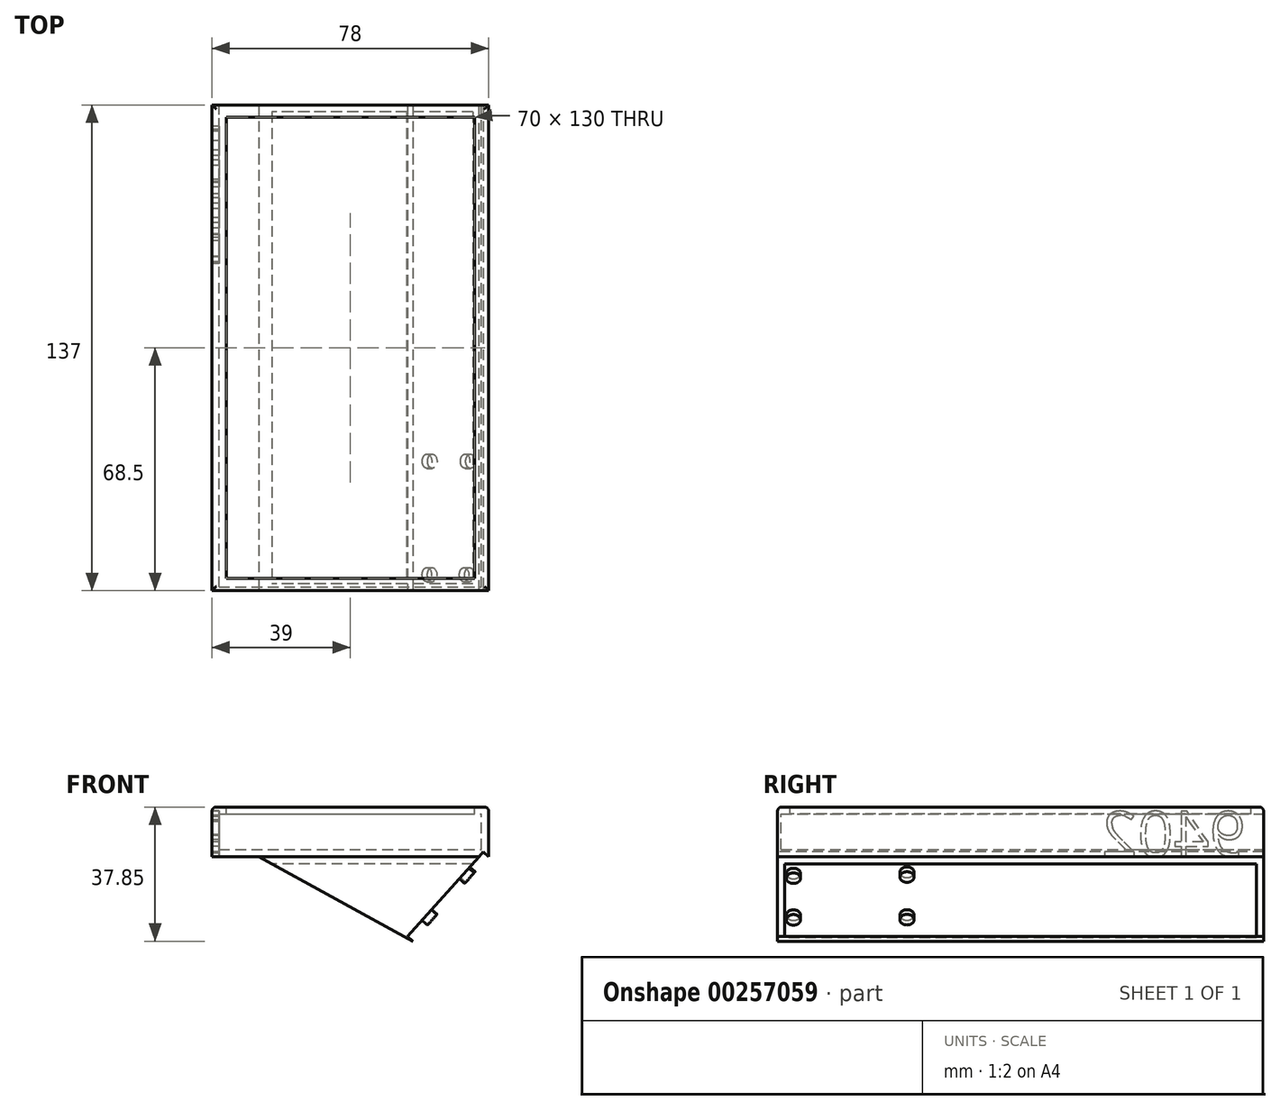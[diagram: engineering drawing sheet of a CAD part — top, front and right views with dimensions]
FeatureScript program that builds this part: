
annotation { "Feature Type Name" : "Feature", "Feature Type Description" : "" }
export const myFeature = defineFeature(function(context is Context, id is Id, definition is map)
    precondition{}
    {
        {
            var Q0;
            Q0=qCreatedBy(makeId("Top.planeOp"),FACE);
            var sketch = newSketch(context, id + "F0", { "sketchPlane" : qUnion([Q0])});
            skLineSegment(sketch, "E0.bottom", {"start": v(39, 68.5) * mm, "end": v(-39, 68.5) * mm});
            skLineSegment(sketch, "E0.top", {"start": v(39, -68.5) * mm, "end": v(-39, -68.5) * mm});
            skLineSegment(sketch, "E0.left", {"start": v(39, 68.5) * mm, "end": v(39, -68.5) * mm});
            skLineSegment(sketch, "E0.right", {"start": v(-39, 68.5) * mm, "end": v(-39, -68.5) * mm});
            skPoint(sketch, "E0.middle", {"position": v(0, 0) * mm});
            skSolve(sketch);
        }
        {
            var Q0;
            Q0 = qSketchRegion(id + "F0", true);
            extrude(context, id + "F1", {"entities" : qUnion([Q0]), "endBound" : BoundingType.SYMMETRIC, "depth" : 14 * mm});
        }
        {
            var Q0;
            Q0=makeQuery(id+"F1.opExtrude","SWEPT_FACE",FACE,{"disambiguationData":[OSD([sQuery(id+"F0.wireOp",EDGE,"E0.top")])]});
            var sketch = newSketch(context, id + "F2", { "sketchPlane" : qUnion([Q0])});
            skLineSegment(sketch, "E1", {"start": v(39, -7) * mm, "end": v(17.67, -30.85) * mm});
            skLineSegment(sketch, "E2", {"start": v(17.67, -30.85) * mm, "end": v(-25.8, -7) * mm});
            skSolve(sketch);
        }
        {
            var Q0;
            Q0 = qSketchRegion(id + "F2", true);
            var Q1;
            {var subQ0=sQuery(id+"F2.wireOp",EDGE,"E1");Q1=makeQuery(id+"F2.imprint","IMPRINT",FACE,{"disambiguationData":[TD([[makeQuery(id+"F2.imprint","IMPRINT",EDGE,{"derivedFrom":subQ0}),-1.0]])]});}
            extrude(context, id + "F3", {"entities" : qUnion([Q0, Q1]), "oppositeDirection" : true, "depth" : 137 * mm});
        }
        {
            var Q0;
            Q0=makeQuery(id+"F1.opExtrude","CAP_FACE",FACE,{"disambiguationData":[OSD([sQuery(id+"F0.wireOp",EDGE,"E0.bottom"),sQuery(id+"F0.wireOp",EDGE,"E0.top"),sQuery(id+"F0.wireOp",EDGE,"E0.left"),sQuery(id+"F0.wireOp",EDGE,"E0.right")])],"isStart":false});
            var sketch = newSketch(context, id + "F4", { "sketchPlane" : qUnion([Q0])});
            skLineSegment(sketch, "E3.bottom", {"start": v(35, -65) * mm, "end": v(-35, -65) * mm});
            skLineSegment(sketch, "E3.top", {"start": v(35, 65) * mm, "end": v(-35, 65) * mm});
            skLineSegment(sketch, "E3.left", {"start": v(35, -65) * mm, "end": v(35, 65) * mm});
            skLineSegment(sketch, "E3.right", {"start": v(-35, -65) * mm, "end": v(-35, 65) * mm});
            skPoint(sketch, "E3.middle", {"position": v(0, 0) * mm});
            skSolve(sketch);
        }
        {
            var Q0;
            Q0 = qSketchRegion(id + "F4", true);
            extrude(context, id + "F5", {"entities" : qUnion([Q0]), "operationType" : NewBodyOperationType.REMOVE, "oppositeDirection" : true, "depth" : 12 * mm});
        }
        {
            var Q0;
            Q0=makeQuery(id+"F1.opExtrude","SWEPT_FACE",FACE,{"disambiguationData":[OSD([sQuery(id+"F0.wireOp",EDGE,"E0.bottom")])]});
            var sketch = newSketch(context, id + "F6", { "sketchPlane" : qUnion([Q0])});
            skLineSegment(sketch, "E4.bottom", {"start": v(37, -5) * mm, "end": v(-37, -5) * mm});
            skLineSegment(sketch, "E4.top", {"start": v(37, 5) * mm, "end": v(-37, 5) * mm});
            skLineSegment(sketch, "E4.left", {"start": v(37, -5) * mm, "end": v(37, 5) * mm});
            skLineSegment(sketch, "E4.right", {"start": v(-37, -5) * mm, "end": v(-37, 5) * mm});
            skPoint(sketch, "E4.middle", {"position": v(0, 0) * mm});
            skSolve(sketch);
        }
        {
            var Q0;
            Q0 = qSketchRegion(id + "F6", true);
            extrude(context, id + "F7", {"entities" : qUnion([Q0]), "operationType" : NewBodyOperationType.REMOVE, "oppositeDirection" : true, "depth" : 136 * mm});
        }
        {
            var Q0;
            Q0=makeQuery(id+"F3.opExtrude","SWEPT_FACE",FACE,{"disambiguationData":[OSD([sQuery(id+"F2.wireOp",EDGE,"E2")])]});
            shell(context, id + "F8", {"entities" : qUnion([Q0]), "thickness" : 2 * mm});
        }
        {
            var Q0;
            Q0=makeQuery(id+"F3.opExtrude","SWEPT_FACE",FACE,{"disambiguationData":[OSD([sQuery(id+"F2.wireOp",EDGE,"E1")])]});
            var sketch = newSketch(context, id + "F9", { "sketchPlane" : qUnion([Q0])});
            skCircle(sketch, "E5", {"center": v(0, -3.22) * mm, "radius": 2 * mm});
            skCircle(sketch, "E6", {"center": v(0, 12.78) * mm, "radius": 2 * mm});
            skLineSegment(sketch, "E7", {"start": v(0, -3.22) * mm, "end": v(68.5, -3.22) * mm, "construction": true});
            skLineSegment(sketch, "E8", {"start": v(0, 12.78) * mm, "end": v(68.5, 12.78) * mm, "construction": true});
            skCircle(sketch, "E9", {"center": v(32, -3.07) * mm, "radius": 2 * mm});
            skCircle(sketch, "E10", {"center": v(32, 13.07) * mm, "radius": 2 * mm});
            skCircle(sketch, "E11", {"center": v(64, -3.13) * mm, "radius": 2 * mm});
            skCircle(sketch, "E12", {"center": v(64, 12.62) * mm, "radius": 2 * mm});
            skCircle(sketch, "E13.MirrorC", {"center": v(-32, -3.07) * mm, "radius": 2 * mm});
            skCircle(sketch, "E14.MirrorC", {"center": v(-64, -3.13) * mm, "radius": 2 * mm});
            skCircle(sketch, "E15.MirrorC", {"center": v(-64, 12.62) * mm, "radius": 2 * mm});
            skCircle(sketch, "E16.MirrorC", {"center": v(-32, 13.07) * mm, "radius": 2 * mm});
            skSolve(sketch);
        }
        {
            var Q0;
            Q0=makeQuery(id+"F9.imprint","IMPRINT",FACE,{"disambiguationData":[TD([[makeQuery(id+"F9.imprint","IMPRINT",EDGE,{"derivedFrom":sQuery(id+"F9.wireOp",EDGE,"E11")}),1.0]])]});
            var Q1;
            Q1=makeQuery(id+"F9.imprint","IMPRINT",FACE,{"disambiguationData":[TD([[makeQuery(id+"F9.imprint","IMPRINT",EDGE,{"derivedFrom":sQuery(id+"F9.wireOp",EDGE,"E12")}),1.0]])]});
            var Q2;
            Q2=makeQuery(id+"F9.imprint","IMPRINT",FACE,{"disambiguationData":[TD([[makeQuery(id+"F9.imprint","IMPRINT",EDGE,{"derivedFrom":sQuery(id+"F9.wireOp",EDGE,"E10")}),1.0]])]});
            var Q3;
            Q3=makeQuery(id+"F9.imprint","IMPRINT",FACE,{"disambiguationData":[TD([[makeQuery(id+"F9.imprint","IMPRINT",EDGE,{"derivedFrom":sQuery(id+"F9.wireOp",EDGE,"E9")}),1.0]])]});
            var Q4;
            Q4=makeQuery(id+"F9.imprint","IMPRINT",FACE,{"disambiguationData":[TD([[makeQuery(id+"F9.imprint","IMPRINT",EDGE,{"derivedFrom":sQuery(id+"F9.wireOp",EDGE,"E5")}),1.0]])]});
            var Q5;
            Q5=makeQuery(id+"F9.imprint","IMPRINT",FACE,{"disambiguationData":[TD([[makeQuery(id+"F9.imprint","IMPRINT",EDGE,{"derivedFrom":sQuery(id+"F9.wireOp",EDGE,"E6")}),1.0]])]});
            var Q6;
            Q6=makeQuery(id+"F9.imprint","IMPRINT",FACE,{"disambiguationData":[TD([[makeQuery(id+"F9.imprint","IMPRINT",EDGE,{"derivedFrom":sQuery(id+"F9.wireOp",EDGE,"E16.MirrorC")}),-1.0]])]});
            var Q7;
            Q7=makeQuery(id+"F9.imprint","IMPRINT",FACE,{"disambiguationData":[TD([[makeQuery(id+"F9.imprint","IMPRINT",EDGE,{"derivedFrom":sQuery(id+"F9.wireOp",EDGE,"E13.MirrorC")}),-1.0]])]});
            var Q8;
            Q8=makeQuery(id+"F9.imprint","IMPRINT",FACE,{"disambiguationData":[TD([[makeQuery(id+"F9.imprint","IMPRINT",EDGE,{"derivedFrom":sQuery(id+"F9.wireOp",EDGE,"E14.MirrorC")}),-1.0]])]});
            var Q9;
            Q9=makeQuery(id+"F9.imprint","IMPRINT",FACE,{"disambiguationData":[TD([[makeQuery(id+"F9.imprint","IMPRINT",EDGE,{"derivedFrom":sQuery(id+"F9.wireOp",EDGE,"E15.MirrorC")}),-1.0]])]});
            extrude(context, id + "F10", {"entities" : qUnion([Q0, Q1, Q2, Q3, Q4, Q5, Q6, Q7, Q8, Q9]), "operationType" : NewBodyOperationType.REMOVE, "oppositeDirection" : true, "depth" : 2 * mm});
        }
        {
            var Q0;
            Q0=makeQuery(id+"F1.opExtrude","CAP_EDGE",EDGE,{"disambiguationData":[OSD([sQuery(id+"F0.wireOp",EDGE,"E0.right")])],"isStart":false});
            var Q1;
            Q1=makeQuery(id+"F1.opExtrude","CAP_EDGE",EDGE,{"disambiguationData":[OSD([sQuery(id+"F0.wireOp",EDGE,"E0.top")])],"isStart":false});
            var Q2;
            Q2=makeQuery(id+"F1.opExtrude","CAP_EDGE",EDGE,{"disambiguationData":[OSD([sQuery(id+"F0.wireOp",EDGE,"E0.left")])],"isStart":false});
            var Q3;
            Q3=makeQuery(id+"F1.opExtrude","CAP_EDGE",EDGE,{"disambiguationData":[OSD([sQuery(id+"F0.wireOp",EDGE,"E0.bottom")])],"isStart":false});
            fillet(context, id + "F11", {"entities" : qUnion([Q0, Q1, Q2, Q3]), "radius" : 1.2 * mm, "tangentPropagation" : true, "allowEdgeOverflow" : false});
        }
        {
            var Q0;
            Q0=makeQuery(id+"F1.opExtrude","SWEPT_FACE",FACE,{"disambiguationData":[OSD([sQuery(id+"F0.wireOp",EDGE,"E0.right")])]});
            var sketch = newSketch(context, id + "F12", { "sketchPlane" : qUnion([Q0])});
            skText(sketch, "E17", { "text": "9402", "fontName": "OpenSans-Regular.ttf"});
            const initialGuessF12  = {"E17": [-0.06343, -0.007, 1, 0, 0.0128]};
            skSetInitialGuess(sketch, initialGuessF12);
            skSolve(sketch);
        }
        {
            var Q0;
            Q0 = qSketchRegion(id + "F12", true);
            extrude(context, id + "F13", {"entities" : qUnion([Q0]), "operationType" : NewBodyOperationType.REMOVE, "oppositeDirection" : true, "depth" : 2 * mm});
        }
    });
